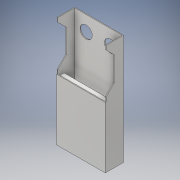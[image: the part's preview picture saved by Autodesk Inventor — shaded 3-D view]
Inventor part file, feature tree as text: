
AUTODESK INVENTOR PART (.ipt)
format: ipt  version: 2018 (Build 220112000, 112)  size: 162,816 bytes
history: native  units: in
note: dims shown in document units (in); Inventor stores cm internally (conversion verified against a paired STEP export)
features: extrude x4, sketch x4, shell x1, direct_edit x1, move_body x1
ambient origin geometry x8: Origin, YZ Plane, XZ Plane, XY Plane, X Axis, Y Axis, Z Axis, Center Point
bodies: Solid1 (feature_tree)
feature tree (11):
  extrude  "Extrusion1"  Depth=0.1772in
  shell  "Shell1"  Thickness=1.063in
  extrude  "Extrusion2"  Depth=0.4724in
  extrude  "Extrusion3"  Depth=0.0079in
  extrude  "Extrusion4"  Depth=0.0807in
  direct_edit  "Direct Edit1"
  sketch  "Sketch1"  dims[d0=0.4724in d1=0.1772in d2=1.063in d3=0.0in]
  sketch  "Sketch2"  dims[d4=0.0079in d5=0.4724in]
  sketch  "Sketch3"  dims[d6=0.0079in d7=0.0394in]
  sketch  "Sketch4"  dims[d9=0.0394in d12=0.0807in d15=0.0807in d16=0.2323in d17=0.0807in d18=1.063in d19=0.0in d20=0.1181in d21=0.1457in d22=0.1181in d23=0.1181in d24=1.063in d25=0.0in d26=0.4567in d27=0.0591in d28=0.0394in d29=0.5709in d30=0.0in d31=0.0in d32=0.0in d33=0.0in d34=-0.0591in]
  move_body  "Move1"
